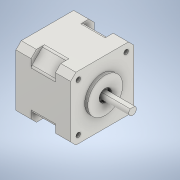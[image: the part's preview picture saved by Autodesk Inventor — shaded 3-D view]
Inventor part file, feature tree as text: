
AUTODESK INVENTOR PART (.ipt)
format: ipt  version: 2021 (Build 250183000, 183)  size: 232,960 bytes
history: native  units: mm
features: extrude x8, sketch x7, chamfer x1, fillet x1
ambient origin geometry x8: Origin, YZ Plane, XZ Plane, XY Plane, X Axis, Y Axis, Z Axis, Center Point
bodies: Volumenkörper1 (feature_tree)
feature tree (17):
  extrude  "Extrusion1"  Depth=41.5mm
  chamfer  "Fase1"  Distance=10.0mm
  extrude  "Extrusion5"  Depth=41.5mm
  extrude  "Extrusion6"  Depth=8.0mm
  fillet  "Rundung1"  Radius=8.0mm
  sketch  "Skizze7"  dims[d22=40.0mm d24=360.0deg d26=16.0mm d27=0.0mm]
  extrude  "Extrusion7"  Depth=16.0mm TaperAngle=0.0deg
  extrude  "Extrusion8"  Depth=41.5mm
  extrude  "Extrusion9"  Depth=10.0mm TaperAngle=0.0deg
  extrude  "Extrusion10"  Depth=8.0mm
  extrude  "Extrusion11"  Depth=2.0mm TaperAngle=0.0deg
  sketch  "Skizze2"  dims[d0=41.5mm d1=41.5mm d2=10.0mm d3=0.0mm]
  sketch  "Skizze5"  dims[d8=3.5mm d9=2.0mm d10=45.0deg d11=41.5mm]
  sketch  "Skizze6"  dims[d12=41.5mm d20=8.0mm d21=8.0mm]
  sketch  "Skizze8"  dims[d28=41.5mm d29=41.5mm]
  sketch  "Skizze9"  dims[d30=40.0mm d32=360.0deg d34=10.0mm d35=0.0mm]
  sketch  "Skizze10"  dims[d36=2.0mm d37=23.0mm d38=2.0mm d39=0.0mm d40=8.0mm d41=2.0mm d42=0.0mm d43=5.0mm d44=0.5mm d45=20.0mm d46=0.0mm d47=2.0mm d48=10.0mm d49=15.0mm d50=4.0mm d51=0.0mm d61=3.0mm d62=3.0mm d67=15.75mm d68=15.75mm d69=3.0mm d70=3.0mm d71=15.75mm d72=15.75mm d73=8.0mm d74=0.0mm]
